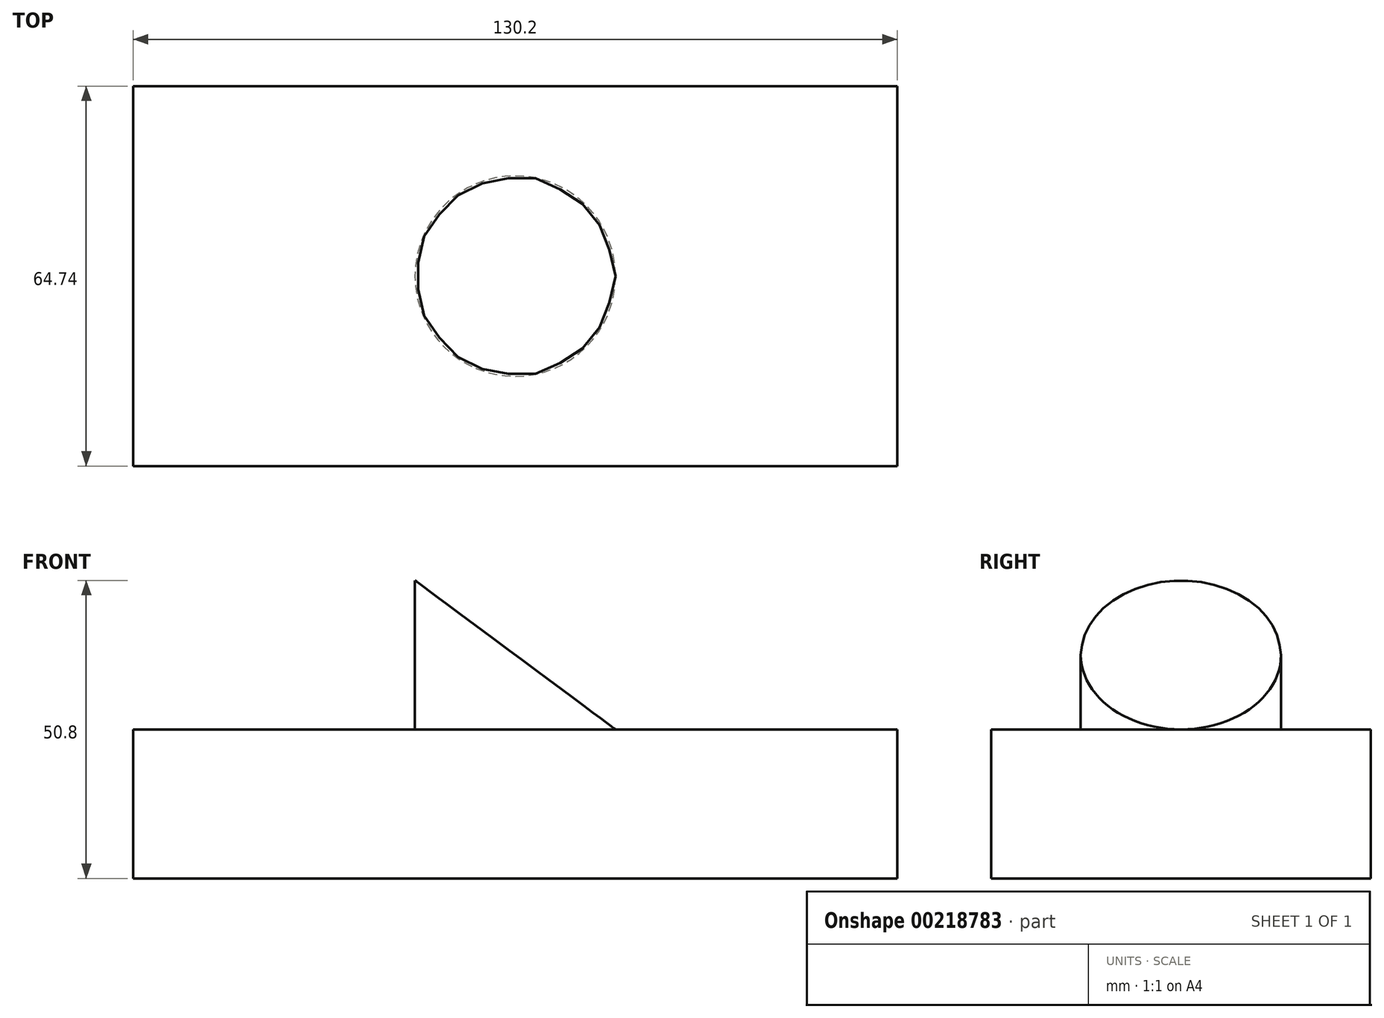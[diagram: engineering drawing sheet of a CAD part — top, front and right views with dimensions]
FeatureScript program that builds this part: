
annotation { "Feature Type Name" : "Feature", "Feature Type Description" : "" }
export const myFeature = defineFeature(function(context is Context, id is Id, definition is map)
    precondition{}
    {
        {
            var Q0;
            Q0=qCreatedBy(makeId("Top.planeOp"),FACE);
            var sketch = newSketch(context, id + "F0", { "sketchPlane" : qUnion([Q0])});
            skLineSegment(sketch, "E0.bottom", {"start": v(65.1, 32.37) * mm, "end": v(-65.1, 32.37) * mm});
            skLineSegment(sketch, "E0.top", {"start": v(65.1, -32.37) * mm, "end": v(-65.1, -32.37) * mm});
            skLineSegment(sketch, "E0.left", {"start": v(65.1, 32.37) * mm, "end": v(65.1, -32.37) * mm});
            skLineSegment(sketch, "E0.right", {"start": v(-65.1, 32.37) * mm, "end": v(-65.1, -32.37) * mm});
            skPoint(sketch, "E0.middle", {"position": v(0, 0) * mm});
            skSolve(sketch);
        }
        {
            var Q0;
            Q0 = qSketchRegion(id + "F0", true);
            extrude(context, id + "F1", {"entities" : qUnion([Q0]), "depth" : 25.4 * mm});
        }
        {
            var Q0;
            Q0=makeQuery(id+"F1.opExtrude","CAP_FACE",FACE,{"disambiguationData":[OSD([sQuery(id+"F0.wireOp",EDGE,"E0.bottom"),sQuery(id+"F0.wireOp",EDGE,"E0.top"),sQuery(id+"F0.wireOp",EDGE,"E0.left"),sQuery(id+"F0.wireOp",EDGE,"E0.right")])],"isStart":false});
            var sketch = newSketch(context, id + "F2", { "sketchPlane" : qUnion([Q0])});
            skSolve(sketch);
        }
        {
            var Q0;
            Q0=makeQuery(id+"F2.imprint","IMPRINT",FACE,{"disambiguationData":[TD([[makeQuery(id+"F2.imprint","IMPRINT",EDGE,{"derivedFrom":makeQuery(id+"F1.opExtrude","CAP_EDGE",EDGE,{"disambiguationData":[OSD([sQuery(id+"F0.wireOp",EDGE,"E0.bottom")])],"isStart":false})}),1.0]])]});
            var sketch = newSketch(context, id + "F3", { "sketchPlane" : qUnion([Q0])});
            skCircle(sketch, "E1", {"center": v(0, 0) * mm, "radius": 17.08 * mm});
            skSolve(sketch);
        }
        {
            var Q0;
            Q0=makeQuery(id+"F3.imprint","IMPRINT",FACE,{"disambiguationData":[TD([[makeQuery(id+"F3.imprint","IMPRINT",EDGE,{"derivedFrom":sQuery(id+"F3.wireOp",EDGE,"E1")}),1.0]])]});
            var Q1;
            Q1=sQuery(id+"F3.wireOp",EDGE,"E1");
            extrude(context, id + "F4", {"entities" : qUnion([Q0]), "operationType" : NewBodyOperationType.ADD, "surfaceEntities" : qUnion([Q1]), "depth" : 25.4 * mm});
        }
        {
            var Q0;
            Q0=qCreatedBy(makeId("Front.planeOp"),FACE);
            var sketch = newSketch(context, id + "F5", { "sketchPlane" : qUnion([Q0])});
            skLineSegment(sketch, "E2.0", {"start": v(-17.08, 50.8) * mm, "end": v(17.08, 50.8) * mm});
            skLineSegment(sketch, "E3", {"start": v(17.08, 50.8) * mm, "end": v(17.08, 25.4) * mm});
            skLineSegment(sketch, "E4", {"start": v(-17.08, 50.8) * mm, "end": v(17.08, 25.4) * mm});
            skSolve(sketch);
        }
        {
            var Q0;
            Q0 = qSketchRegion(id + "F5", true);
            extrude(context, id + "F6", {"entities" : qUnion([Q0]), "operationType" : NewBodyOperationType.REMOVE, "endBound" : BoundingType.SYMMETRIC, "oppositeDirection" : true, "depth" : 113.8 * mm});
        }
    });
